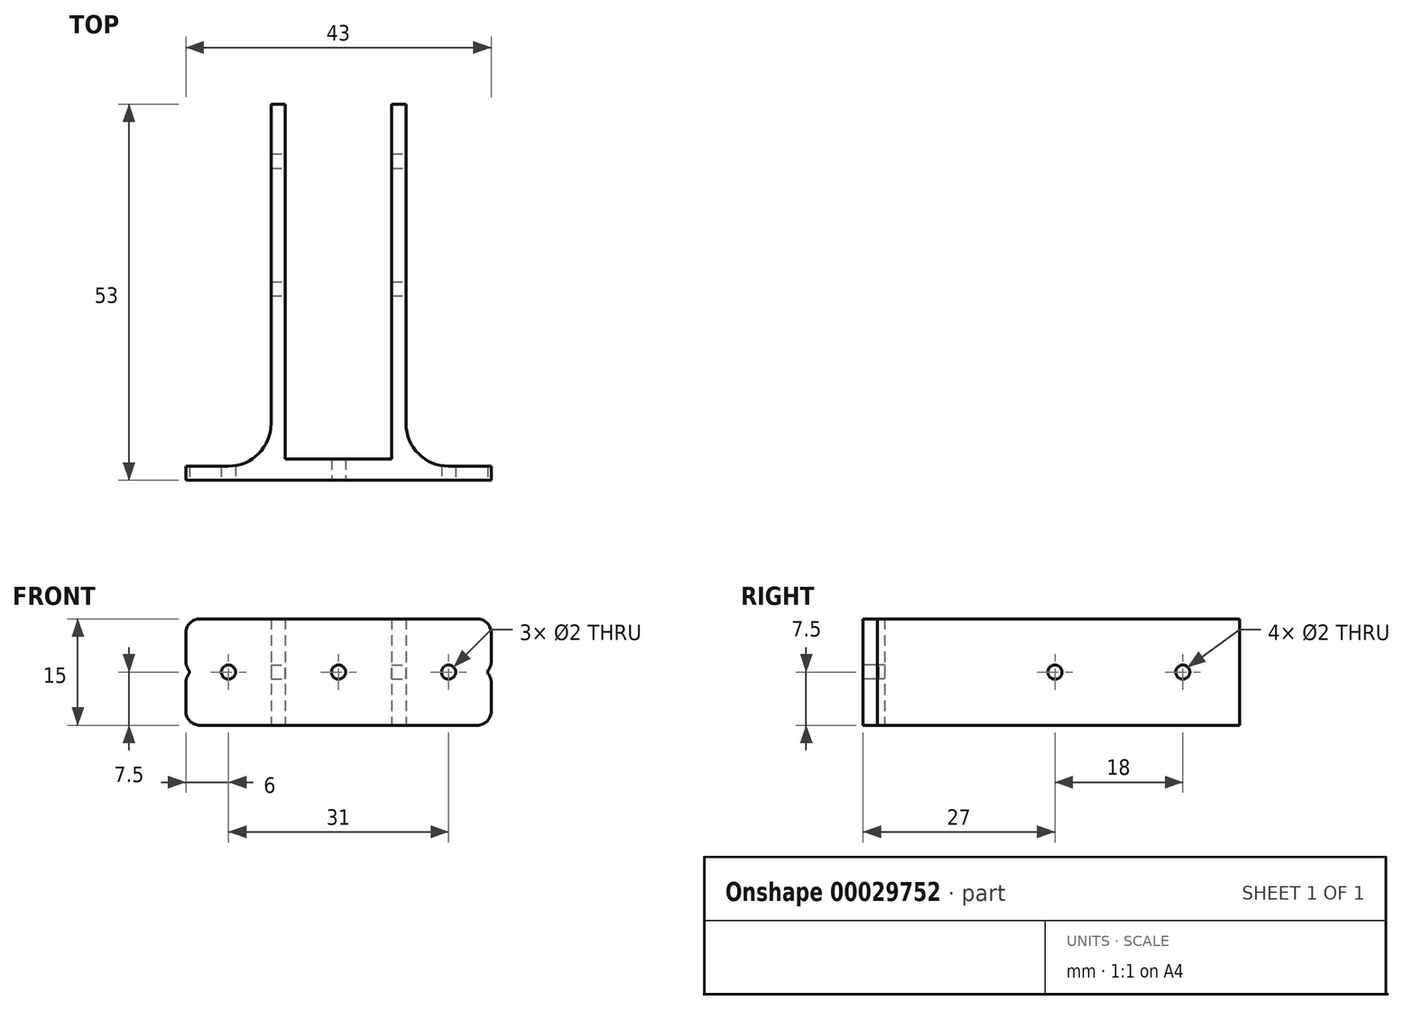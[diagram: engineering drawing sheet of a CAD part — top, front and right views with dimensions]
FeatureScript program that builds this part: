
annotation { "Feature Type Name" : "Feature", "Feature Type Description" : "" }
export const myFeature = defineFeature(function(context is Context, id is Id, definition is map)
    precondition{}
    {
        {
            var Q0;
            Q0=qCreatedBy(makeId("Top.planeOp"),FACE);
            var sketch = newSketch(context, id + "F0", { "sketchPlane" : qUnion([Q0])});
            skLineSegment(sketch, "E0.top", {"start": v(0, 53) * mm, "end": v(-2, 53) * mm});
            skLineSegment(sketch, "E0.left", {"start": v(0, 2) * mm, "end": v(0, 53) * mm});
            skLineSegment(sketch, "E0.right", {"start": v(-19, 2) * mm, "end": v(-19, 53) * mm});
            skLineSegment(sketch, "E1.top", {"start": v(-17, 3) * mm, "end": v(-2, 3) * mm});
            skLineSegment(sketch, "E1.left", {"start": v(-17, 53) * mm, "end": v(-17, 3) * mm});
            skLineSegment(sketch, "E1.right", {"start": v(-2, 53) * mm, "end": v(-2, 3) * mm});
            skLineSegment(sketch, "E2.trimOffspring", {"start": v(-17, 53) * mm, "end": v(-19, 53) * mm});
            skLineSegment(sketch, "E3", {"start": v(-19, 0) * mm, "end": v(0, 0) * mm});
            skLineSegment(sketch, "E4", {"start": v(-19, 0) * mm, "end": v(-31, 0) * mm});
            skLineSegment(sketch, "E5", {"start": v(-31, 0) * mm, "end": v(-31, 2) * mm});
            skLineSegment(sketch, "E6", {"start": v(-31, 2) * mm, "end": v(-19, 2) * mm});
            skLineSegment(sketch, "E7", {"start": v(0, 2) * mm, "end": v(12, 2) * mm});
            skLineSegment(sketch, "E8", {"start": v(12, 2) * mm, "end": v(12, 0) * mm});
            skLineSegment(sketch, "E9", {"start": v(12, 0) * mm, "end": v(0, 0) * mm});
            skSolve(sketch);
        }
        {
            var Q0;
            Q0=makeQuery(id+"F0.imprint","IMPRINT",FACE,{"disambiguationData":[TD([[makeQuery(id+"F0.imprint","IMPRINT",EDGE,{"derivedFrom":sQuery(id+"F0.wireOp",EDGE,"E0.top")}),1.0]])]});
            extrude(context, id + "F1", {"entities" : qUnion([Q0]), "depth" : 15 * mm});
        }
        {
            var Q0;
            Q0=makeQuery(id+"F1.opExtrude","SWEPT_FACE",FACE,{"disambiguationData":[OSD([sQuery(id+"F0.wireOp",EDGE,"E0.left")])]});
            var sketch = newSketch(context, id + "F2", { "sketchPlane" : qUnion([Q0])});
            skCircle(sketch, "E10", {"center": v(27, 7.5) * mm, "radius": 1 * mm});
            skCircle(sketch, "E11", {"center": v(45, 7.5) * mm, "radius": 1 * mm});
            skSolve(sketch);
        }
        {
            var Q0;
            Q0=qSketchRegion(id+"F2",true);
            extrude(context, id + "F3", {"entities" : qUnion([Q0]), "operationType" : NewBodyOperationType.REMOVE, "oppositeDirection" : true, "depth" : 25 * mm});
        }
        {
            var Q0;
            Q0=makeQuery(id+"F1.opExtrude","SWEPT_EDGE",EDGE,{"disambiguationData":[OSD([sQuery(id+"F0.wireOp",EDGE,"E0.left"),sQuery(id+"F0.wireOp",EDGE,"E7")])]});
            var Q1;
            Q1=makeQuery(id+"F1.opExtrude","SWEPT_EDGE",EDGE,{"disambiguationData":[OSD([sQuery(id+"F0.wireOp",EDGE,"E0.right"),sQuery(id+"F0.wireOp",EDGE,"E6")])]});
            fillet(context, id + "F4", {"entities" : qUnion([Q0, Q1]), "radius" : 6 * mm, "tangentPropagation" : true, "allowEdgeOverflow" : false});
        }
        {
            var Q0;
            Q0=makeQuery(id+"F1.opExtrude","SWEPT_FACE",FACE,{"disambiguationData":[OSD([sQuery(id+"F0.wireOp",EDGE,"E3"),sQuery(id+"F0.wireOp",EDGE,"E4"),sQuery(id+"F0.wireOp",EDGE,"E9")])]});
            var sketch = newSketch(context, id + "F5", { "sketchPlane" : qUnion([Q0])});
            skCircle(sketch, "E12", {"center": v(-9.5, 7.5) * mm, "radius": 1 * mm});
            skCircle(sketch, "E13", {"center": v(-25, 7.5) * mm, "radius": 1 * mm});
            skCircle(sketch, "E14", {"center": v(6, 7.5) * mm, "radius": 1 * mm});
            skLineSegment(sketch, "E15.0", {"start": v(12, 15) * mm, "end": v(12, 0) * mm});
            skCircle(sketch, "E16", {"center": v(-31, 7.5) * mm, "radius": 0.5 * mm});
            skCircle(sketch, "E17", {"center": v(12, 7.5) * mm, "radius": 0.5 * mm});
            skLineSegment(sketch, "E18.0", {"start": v(12, 15) * mm, "end": v(-31, 15) * mm});
            skSolve(sketch);
        }
        {
            var Q0;
            Q0=qSketchRegion(id+"F5",true);
            extrude(context, id + "F6", {"entities" : qUnion([Q0]), "operationType" : NewBodyOperationType.REMOVE, "oppositeDirection" : true, "depth" : 25 * mm});
        }
        {
            var Q0;
            Q0=makeQuery(id+"F6.boolean.opBoolean","INTERSECT",EDGE,{"disambiguationData":[OD(1.0)],"derivedFrom":[makeQuery(id+"F1.opExtrude","SWEPT_FACE",FACE,{"disambiguationData":[OSD([sQuery(id+"F0.wireOp",EDGE,"E5")])]}),makeQuery(id+"F6.opExtrude","SWEPT_FACE",FACE,{"disambiguationData":[OSD([sQuery(id+"F5.wireOp",EDGE,"E16")])]})]});
            var Q1;
            Q1=makeQuery(id+"F6.boolean.opBoolean","INTERSECT",EDGE,{"disambiguationData":[OD(0.0)],"derivedFrom":[makeQuery(id+"F1.opExtrude","SWEPT_FACE",FACE,{"disambiguationData":[OSD([sQuery(id+"F0.wireOp",EDGE,"E5")])]}),makeQuery(id+"F6.opExtrude","SWEPT_FACE",FACE,{"disambiguationData":[OSD([sQuery(id+"F5.wireOp",EDGE,"E16")])]})]});
            var Q2;
            Q2=makeQuery(id+"F6.boolean.opBoolean","INTERSECT",EDGE,{"disambiguationData":[OD(1.0)],"derivedFrom":[makeQuery(id+"F1.opExtrude","SWEPT_FACE",FACE,{"disambiguationData":[OSD([sQuery(id+"F0.wireOp",EDGE,"E8")])]}),makeQuery(id+"F6.opExtrude","SWEPT_FACE",FACE,{"disambiguationData":[OSD([sQuery(id+"F5.wireOp",EDGE,"E17")])]})]});
            var Q3;
            Q3=makeQuery(id+"F6.boolean.opBoolean","INTERSECT",EDGE,{"disambiguationData":[OD(0.0)],"derivedFrom":[makeQuery(id+"F1.opExtrude","SWEPT_FACE",FACE,{"disambiguationData":[OSD([sQuery(id+"F0.wireOp",EDGE,"E8")])]}),makeQuery(id+"F6.opExtrude","SWEPT_FACE",FACE,{"disambiguationData":[OSD([sQuery(id+"F5.wireOp",EDGE,"E17")])]})]});
            var Q4;
            Q4=makeQuery(id+"F1.opExtrude","CAP_EDGE",EDGE,{"disambiguationData":[OSD([sQuery(id+"F0.wireOp",EDGE,"E5")])],"isStart":false});
            var Q5;
            Q5=makeQuery(id+"F1.opExtrude","CAP_EDGE",EDGE,{"disambiguationData":[OSD([sQuery(id+"F0.wireOp",EDGE,"E5")])],"isStart":true});
            var Q6;
            Q6=makeQuery(id+"F1.opExtrude","CAP_EDGE",EDGE,{"disambiguationData":[OSD([sQuery(id+"F0.wireOp",EDGE,"E8")])],"isStart":false});
            var Q7;
            Q7=makeQuery(id+"F1.opExtrude","CAP_EDGE",EDGE,{"disambiguationData":[OSD([sQuery(id+"F0.wireOp",EDGE,"E8")])],"isStart":true});
            fillet(context, id + "F7", {"entities" : qUnion([Q0, Q1, Q2, Q3, Q4, Q5, Q6, Q7]), "radius" : 2 * mm, "tangentPropagation" : true, "allowEdgeOverflow" : false});
        }
    });
